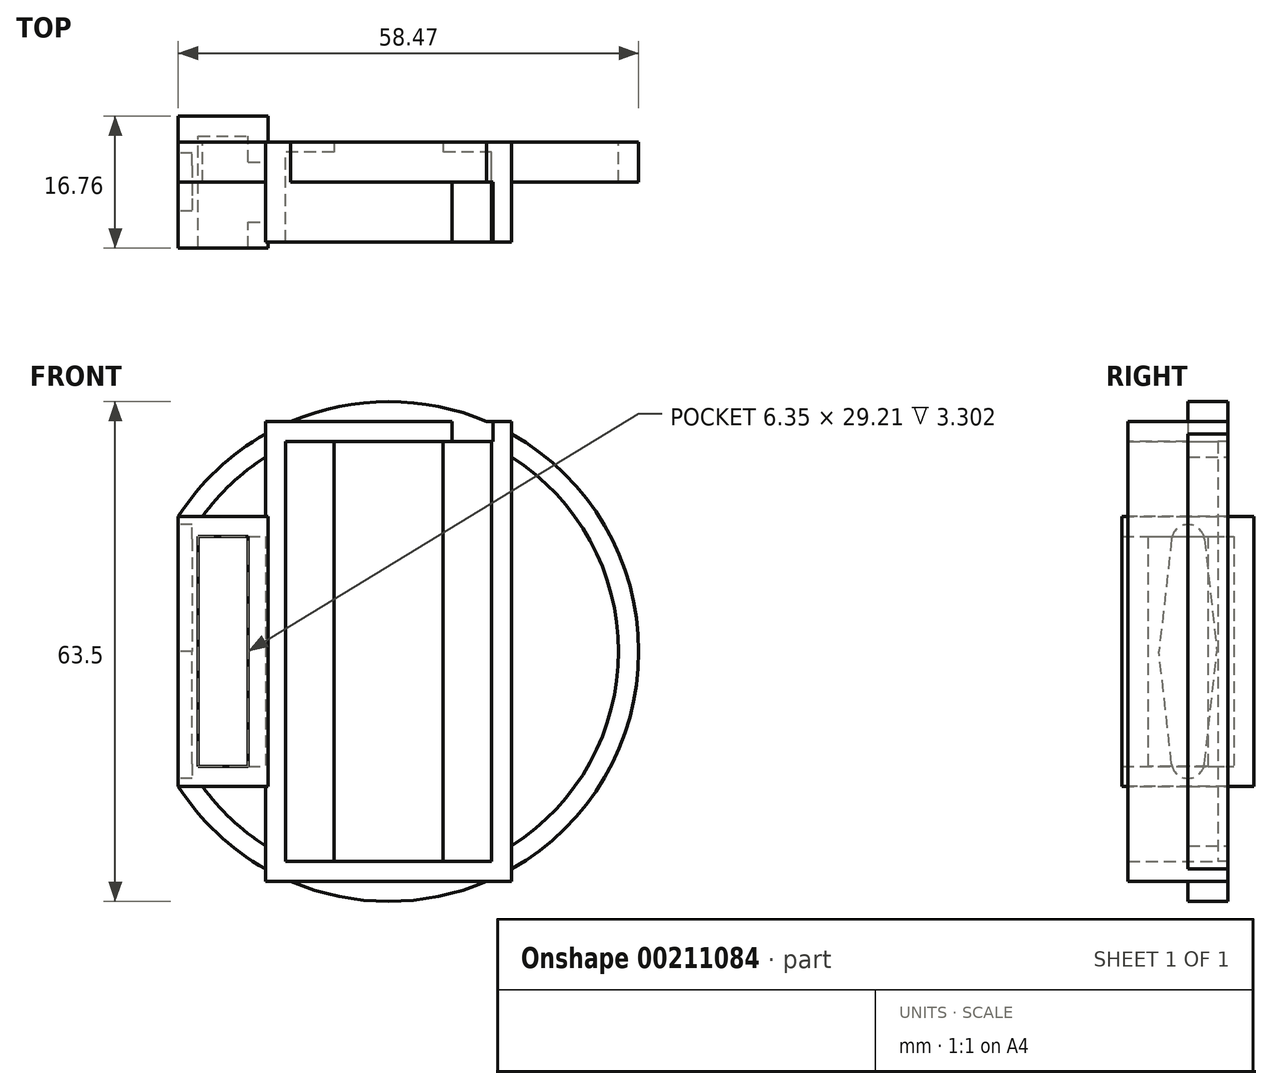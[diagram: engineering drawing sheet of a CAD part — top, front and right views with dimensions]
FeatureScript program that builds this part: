
annotation { "Feature Type Name" : "Feature", "Feature Type Description" : "" }
export const myFeature = defineFeature(function(context is Context, id is Id, definition is map)
    precondition{}
    {
        {
            var Q0;
            Q0=qCreatedBy(makeId("Front.planeOp"),FACE);
            var sketch = newSketch(context, id + "F0", { "sketchPlane" : qUnion([Q0])});
            skLineSegment(sketch, "E0.bottom", {"start": v(13.08, 26.67) * mm, "end": v(-13.08, 26.67) * mm, "construction": true});
            skLineSegment(sketch, "E0.top", {"start": v(13.08, -26.67) * mm, "end": v(-13.08, -26.67) * mm, "construction": true});
            skLineSegment(sketch, "E0.left", {"start": v(13.08, 26.67) * mm, "end": v(13.08, -26.67) * mm, "construction": true});
            skLineSegment(sketch, "E0.right", {"start": v(-13.08, 26.67) * mm, "end": v(-13.08, -26.67) * mm, "construction": true});
            skPoint(sketch, "E0.middle", {"position": v(0, 0) * mm});
            skArc(sketch, "E1", {"start": v(-26.72, -17.14) * mm, "mid": v(31.75, 0) * mm, "end": v(-26.72, 17.15) * mm});
            skLineSegment(sketch, "E2", {"start": v(-26.72, 17.15) * mm, "end": v(-26.72, -17.15) * mm});
            skPoint(sketch, "E3.orphan", {"position": v(-35.05, 17.15) * mm});
            skPoint(sketch, "E4.orphan", {"position": v(-35.05, -17.15) * mm});
            skPoint(sketch, "E5.left.start.orphan", {"position": v(35.05, 17.15) * mm});
            skPoint(sketch, "E5.top.start.orphan", {"position": v(35.05, -17.15) * mm});
            skArc(sketch, "E6.0", {"start": v(-24.18, -16.38) * mm, "mid": v(29.21, 0) * mm, "end": v(-24.18, 16.38) * mm});
            skLineSegment(sketch, "E6.1", {"start": v(-24.18, 16.38) * mm, "end": v(-24.18, -16.38) * mm});
            skSolve(sketch);
        }
        {
            var Q0;
            Q0 = qSketchRegion(id + "F0", true);
            extrude(context, id + "F1", {"entities" : qUnion([Q0]), "depth" : 5.08 * mm});
        }
        {
            var Q0;
            Q0=qCreatedBy(makeId("Front.planeOp"),FACE);
            var sketch = newSketch(context, id + "F2", { "sketchPlane" : qUnion([Q0])});
            skLineSegment(sketch, "E7.bottom", {"start": v(13.08, 26.67) * mm, "end": v(-13.08, 26.67) * mm});
            skLineSegment(sketch, "E7.top", {"start": v(13.08, -26.67) * mm, "end": v(-13.08, -26.67) * mm});
            skLineSegment(sketch, "E7.left", {"start": v(13.08, 26.67) * mm, "end": v(13.08, -26.67) * mm});
            skLineSegment(sketch, "E7.right", {"start": v(-13.08, 26.67) * mm, "end": v(-13.08, -26.67) * mm});
            skPoint(sketch, "E7.middle", {"position": v(0, 0) * mm});
            skLineSegment(sketch, "E8.0", {"start": v(15.62, 29.21) * mm, "end": v(-15.62, 29.21) * mm});
            skLineSegment(sketch, "E8.1", {"start": v(15.62, 29.21) * mm, "end": v(15.62, -29.21) * mm});
            skLineSegment(sketch, "E8.2", {"start": v(15.62, -29.21) * mm, "end": v(-15.62, -29.21) * mm});
            skLineSegment(sketch, "E8.3", {"start": v(-15.62, 29.21) * mm, "end": v(-15.62, -29.21) * mm});
            skSolve(sketch);
        }
        {
            var Q0;
            Q0 = qSketchRegion(id + "F2", true);
            extrude(context, id + "F3", {"entities" : qUnion([Q0]), "operationType" : NewBodyOperationType.ADD, "depth" : 12.7 * mm});
        }
        {
            var Q0;
            Q0=makeQuery(id+"F1.opExtrude","CAP_FACE",FACE,{"disambiguationData":[OSD([sQuery(id+"F0.wireOp",EDGE,"E1")])],"isStart":false});
            var sketch = newSketch(context, id + "F4", { "sketchPlane" : qUnion([Q0])});
            skLineSegment(sketch, "E9.bottom", {"start": v(13.08, 26.67) * mm, "end": v(-13.08, 26.67) * mm});
            skLineSegment(sketch, "E9.top", {"start": v(13.08, -26.67) * mm, "end": v(-13.08, -26.67) * mm});
            skLineSegment(sketch, "E9.left", {"start": v(13.08, 26.67) * mm, "end": v(13.08, -26.67) * mm});
            skLineSegment(sketch, "E9.right", {"start": v(-13.08, 26.67) * mm, "end": v(-13.08, -26.67) * mm});
            skPoint(sketch, "E9.middle", {"position": v(0, 0) * mm});
            skSolve(sketch);
        }
        {
            var Q0;
            {var subQ1=makeQuery(id+"F1.opExtrude","CAP_EDGE",EDGE,{"disambiguationData":[OSD([sQuery(id+"F0.wireOp",EDGE,"E6.0")])],"isStart":false});var subQ10=sQuery(id+"F4.wireOp",EDGE,"E9.bottom");var subQ11=makeQuery(id+"F4.imprint","INTERSECT",VERTEX,{"disambiguationData":[OD(0.0)],"derivedFrom":[subQ1,subQ10]});Q0=makeQuery(id+"F4.imprint","IMPRINT",FACE,{"disambiguationData":[TD([[makeQuery(id+"F4.imprint","IMPRINT",EDGE,{"disambiguationData":[TD([[subQ11,-1.0]])],"derivedFrom":subQ10}),1.0]])]});}
            extrude(context, id + "F5", {"entities" : qUnion([Q0]), "operationType" : NewBodyOperationType.REMOVE, "oppositeDirection" : true, "depth" : 5.08 * mm});
        }
        {
            var Q0;
            Q0=qCreatedBy(makeId("Front.planeOp"),FACE);
            var sketch = newSketch(context, id + "F6", { "sketchPlane" : qUnion([Q0])});
            skLineSegment(sketch, "E10.bottom", {"start": v(13.08, 26.67) * mm, "end": v(-13.08, 26.67) * mm, "construction": true});
            skLineSegment(sketch, "E10.top", {"start": v(13.08, -26.67) * mm, "end": v(-13.08, -26.67) * mm, "construction": true});
            skLineSegment(sketch, "E10.left", {"start": v(13.08, 26.67) * mm, "end": v(13.08, -26.67) * mm, "construction": true});
            skLineSegment(sketch, "E10.right", {"start": v(-13.08, 26.67) * mm, "end": v(-13.08, -26.67) * mm, "construction": true});
            skPoint(sketch, "E10.middle", {"position": v(0, 0) * mm});
            skLineSegment(sketch, "E11.0", {"start": v(15.62, 29.21) * mm, "end": v(-15.62, 29.21) * mm});
            skLineSegment(sketch, "E11.1", {"start": v(15.62, 29.21) * mm, "end": v(15.62, -29.21) * mm});
            skLineSegment(sketch, "E11.2", {"start": v(15.62, -29.21) * mm, "end": v(-15.62, -29.21) * mm});
            skLineSegment(sketch, "E11.3", {"start": v(-15.62, 29.21) * mm, "end": v(-15.62, -29.21) * mm});
            skSolve(sketch);
        }
        {
            var Q0;
            Q0 = qSketchRegion(id + "F6", true);
            var Q1;
            Q1=sQuery(id+"F6.wireOp",EDGE,"E10.bottom");
            var Q2;
            Q2=sQuery(id+"F6.wireOp",EDGE,"E10.right");
            var Q3;
            Q3=sQuery(id+"F6.wireOp",EDGE,"E10.left");
            var Q4;
            Q4=sQuery(id+"F6.wireOp",EDGE,"E10.top");
            extrude(context, id + "F7", {"entities" : qUnion([Q0]), "operationType" : NewBodyOperationType.ADD, "surfaceEntities" : qUnion([Q1, Q2, Q3, Q4]), "depth" : 1.27 * mm});
        }
        {
            var Q0;
            {var subQ0=sQuery(id+"F0.wireOp",EDGE,"E6.1");var subQ1=sQuery(id+"F0.wireOp",EDGE,"E6.0");var subQ2=sQuery(id+"F0.wireOp",EDGE,"E2");var subQ3=sQuery(id+"F0.wireOp",EDGE,"E1");Q0=makeQuery(id+"F3.boolean.opBoolean","SPLIT",FACE,{"disambiguationData":[TD([makeQuery(id+"F1.opExtrude","SWEPT_FACE",FACE,{"disambiguationData":[OSD([subQ3])]}),makeQuery(id+"F1.opExtrude","SWEPT_FACE",FACE,{"disambiguationData":[OSD([subQ2])]}),makeQuery(id+"F1.opExtrude","SWEPT_FACE",FACE,{"disambiguationData":[OSD([subQ1])]}),makeQuery(id+"F1.opExtrude","SWEPT_FACE",FACE,{"disambiguationData":[OSD([subQ0])]}),makeQuery(id+"F3.opExtrude","SWEPT_FACE",FACE,{"disambiguationData":[OSD([sQuery(id+"F2.wireOp",EDGE,"E8.3")])]})])],"derivedFrom":makeQuery(id+"F1.opExtrude","CAP_FACE",FACE,{"disambiguationData":[OSD([subQ3,subQ2,subQ1,subQ0])],"isStart":false})});}
            var sketch = newSketch(context, id + "F8", { "sketchPlane" : qUnion([Q0])});
            skLineSegment(sketch, "E12.bottom", {"start": v(-26.72, 17.15) * mm, "end": v(-15.3, 17.15) * mm});
            skLineSegment(sketch, "E12.top", {"start": v(-26.72, -17.14) * mm, "end": v(-15.3, -17.14) * mm});
            skLineSegment(sketch, "E12.left", {"start": v(-26.72, 17.15) * mm, "end": v(-26.72, -17.14) * mm});
            skLineSegment(sketch, "E12.right", {"start": v(-15.3, 17.15) * mm, "end": v(-15.3, -17.14) * mm});
            skSolve(sketch);
        }
        {
            var Q0;
            Q0 = qSketchRegion(id + "F8", true);
            extrude(context, id + "F9", {"entities" : qUnion([Q0]), "operationType" : NewBodyOperationType.ADD, "endBound" : BoundingType.SYMMETRIC, "depth" : 16.76 * mm});
        }
        {
            var Q0;
            Q0=makeQuery(id+"F9.opExtrude","CAP_FACE",FACE,{"disambiguationData":[OSD([sQuery(id+"F8.wireOp",EDGE,"E12.bottom"),sQuery(id+"F8.wireOp",EDGE,"E12.top"),sQuery(id+"F8.wireOp",EDGE,"E12.left"),sQuery(id+"F8.wireOp",EDGE,"E12.right")])],"isStart":false});
            shell(context, id + "F10", {"entities" : qUnion([Q0]), "thickness" : 2.54 * mm});
        }
        {
            var Q0;
            Q0=makeQuery(id+"F7.opExtrude","CAP_FACE",FACE,{"disambiguationData":[OSD([sQuery(id+"F6.wireOp",EDGE,"E11.0"),sQuery(id+"F6.wireOp",EDGE,"E11.1"),sQuery(id+"F6.wireOp",EDGE,"E11.2"),sQuery(id+"F6.wireOp",EDGE,"E11.3")])],"isStart":false});
            var sketch = newSketch(context, id + "F11", { "sketchPlane" : qUnion([Q0])});
            skLineSegment(sketch, "E13.bottom", {"start": v(6.94, 26.67) * mm, "end": v(-6.94, 26.67) * mm});
            skLineSegment(sketch, "E13.top", {"start": v(6.94, -26.67) * mm, "end": v(-6.94, -26.67) * mm});
            skLineSegment(sketch, "E13.left", {"start": v(6.94, 26.67) * mm, "end": v(6.94, -26.67) * mm});
            skLineSegment(sketch, "E13.right", {"start": v(-6.94, 26.67) * mm, "end": v(-6.94, -26.67) * mm});
            skPoint(sketch, "E13.middle", {"position": v(0, 0) * mm});
            skSolve(sketch);
        }
        {
            var Q0;
            Q0=makeQuery(id+"F11.imprint","IMPRINT",FACE,{"disambiguationData":[TD([[makeQuery(id+"F11.imprint","IMPRINT",EDGE,{"derivedFrom":sQuery(id+"F11.wireOp",EDGE,"E13.bottom")}),1.0]])]});
            extrude(context, id + "F12", {"entities" : qUnion([Q0]), "operationType" : NewBodyOperationType.REMOVE, "oppositeDirection" : true, "depth" : 25.4 * mm});
        }
        {
            var Q0;
            Q0=makeQuery(id+"F3.opExtrude","CAP_FACE",FACE,{"disambiguationData":[OSD([sQuery(id+"F2.wireOp",EDGE,"E7.bottom"),sQuery(id+"F2.wireOp",EDGE,"E7.top"),sQuery(id+"F2.wireOp",EDGE,"E7.left"),sQuery(id+"F2.wireOp",EDGE,"E7.right"),sQuery(id+"F2.wireOp",EDGE,"E8.0"),sQuery(id+"F2.wireOp",EDGE,"E8.1"),sQuery(id+"F2.wireOp",EDGE,"E8.2"),sQuery(id+"F2.wireOp",EDGE,"E8.3")])],"isStart":false});
            var sketch = newSketch(context, id + "F13", { "sketchPlane" : qUnion([Q0])});
            skLineSegment(sketch, "E14.bottom", {"start": v(13.27, 29.21) * mm, "end": v(8.03, 29.21) * mm});
            skLineSegment(sketch, "E14.top", {"start": v(13.27, 26.67) * mm, "end": v(8.03, 26.67) * mm});
            skLineSegment(sketch, "E14.left", {"start": v(13.27, 29.21) * mm, "end": v(13.27, 26.67) * mm});
            skLineSegment(sketch, "E14.right", {"start": v(8.03, 29.21) * mm, "end": v(8.03, 26.67) * mm});
            skSolve(sketch);
        }
        {
            var Q0;
            Q0=makeQuery(id+"F13.imprint","IMPRINT",FACE,{"disambiguationData":[TD([[makeQuery(id+"F13.imprint","IMPRINT",EDGE,{"derivedFrom":sQuery(id+"F13.wireOp",EDGE,"E14.bottom")}),1.0]])]});
            extrude(context, id + "F14", {"entities" : qUnion([Q0]), "operationType" : NewBodyOperationType.REMOVE, "oppositeDirection" : true, "depth" : 7.62 * mm});
        }
        {
            var Q0;
            Q0=makeQuery(id+"F9.boolean.opBoolean","MERGE",FACE,{"derivedFrom":[makeQuery(id+"F1.opExtrude","SWEPT_FACE",FACE,{"disambiguationData":[OSD([sQuery(id+"F0.wireOp",EDGE,"E2")])]}),makeQuery(id+"F9.opExtrude","SWEPT_FACE",FACE,{"disambiguationData":[OSD([sQuery(id+"F8.wireOp",EDGE,"E12.left")])]})]});
            var sketch = newSketch(context, id + "F15", { "sketchPlane" : qUnion([Q0])});
            skLineSegment(sketch, "E15", {"start": v(13.46, 0) * mm, "end": v(-3.3, 0) * mm, "construction": true});
            skPoint(sketch, "E16", {"position": v(5.08, 0) * mm});
            skCircle(sketch, "E17", {"center": v(5.08, 0) * mm, "radius": 3.66 * mm, "construction": true});
            skLineSegment(sketch, "E18.bottom", {"start": v(5.08, -16.13) * mm, "end": v(5.08, -16.13) * mm});
            skLineSegment(sketch, "E18.top", {"start": v(5.08, 16.13) * mm, "end": v(5.08, 16.13) * mm});
            skLineSegment(sketch, "E18.left", {"start": v(7.18, -14.03) * mm, "end": v(7.18, 14.03) * mm, "construction": true});
            skLineSegment(sketch, "E18.right", {"start": v(2.98, -14.03) * mm, "end": v(2.98, 14.03) * mm, "construction": true});
            skPoint(sketch, "E19.visualSharp", {"position": v(7.18, 16.13) * mm});
            skArc(sketch, "E19.filletArc", {"start": v(7.18, 14.03) * mm, "mid": v(6.56, 15.52) * mm, "end": v(5.08, 16.13) * mm});
            skPoint(sketch, "E20.visualSharp", {"position": v(2.98, 16.13) * mm});
            skArc(sketch, "E20.filletArc", {"start": v(5.08, 16.13) * mm, "mid": v(3.6, 15.52) * mm, "end": v(2.98, 14.03) * mm});
            skLineSegment(sketch, "E21", {"start": v(3, 14.27) * mm, "end": v(1.4, 0) * mm});
            skLineSegment(sketch, "E22", {"start": v(5.08, 17.15) * mm, "end": v(5.08, -15.75) * mm, "construction": true});
            skLineSegment(sketch, "E23.MirrorCS", {"start": v(7.16, 14.27) * mm, "end": v(8.76, 0) * mm});
            skLineSegment(sketch, "E24.MirrorCS", {"start": v(-3.3, 0) * mm, "end": v(13.46, 0) * mm, "construction": true});
            skLineSegment(sketch, "E25.MirrorCS", {"start": v(7.16, -14.27) * mm, "end": v(8.76, 0) * mm});
            skLineSegment(sketch, "E26.MirrorCS", {"start": v(3, -14.27) * mm, "end": v(1.4, 0) * mm});
            skPoint(sketch, "E27.visualSharp", {"position": v(7.18, -16.13) * mm});
            skArc(sketch, "E27.filletArc", {"start": v(5.08, -16.13) * mm, "mid": v(6.56, -15.52) * mm, "end": v(7.18, -14.03) * mm});
            skPoint(sketch, "E28.visualSharp", {"position": v(2.98, -16.13) * mm});
            skArc(sketch, "E28.filletArc", {"start": v(2.98, -14.03) * mm, "mid": v(3.6, -15.52) * mm, "end": v(5.08, -16.13) * mm});
            skSolve(sketch);
        }
        {
            var Q0;
            Q0 = qSketchRegion(id + "F15", true);
            extrude(context, id + "F16", {"entities" : qUnion([Q0]), "operationType" : NewBodyOperationType.REMOVE, "oppositeDirection" : true, "depth" : 1.78 * mm});
        }
    });
